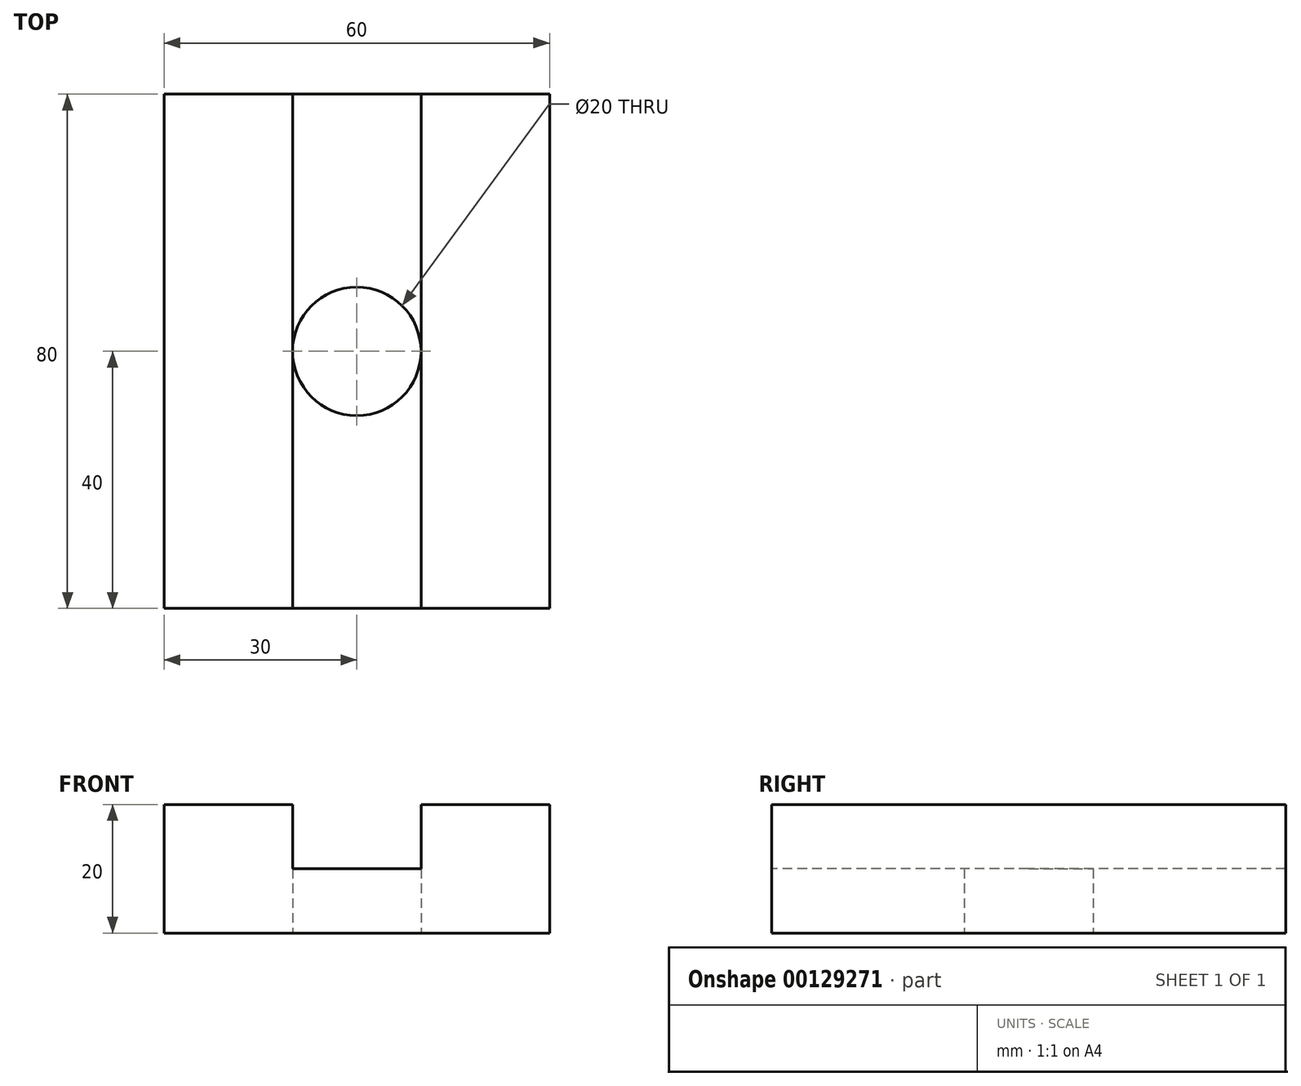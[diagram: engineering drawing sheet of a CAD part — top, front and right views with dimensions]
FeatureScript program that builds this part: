
annotation { "Feature Type Name" : "Feature", "Feature Type Description" : "" }
export const myFeature = defineFeature(function(context is Context, id is Id, definition is map)
    precondition{}
    {
        {
            var Q0;
            Q0=qCreatedBy(makeId("Front.planeOp"),FACE);
            var sketch = newSketch(context, id + "F0", { "sketchPlane" : qUnion([Q0])});
            skLineSegment(sketch, "E0", {"start": v(0, 0) * mm, "end": v(60, 0) * mm});
            skLineSegment(sketch, "E1", {"start": v(60, 0) * mm, "end": v(60, 20) * mm});
            skLineSegment(sketch, "E2", {"start": v(60, 20) * mm, "end": v(40, 20) * mm});
            skLineSegment(sketch, "E3", {"start": v(40, 20) * mm, "end": v(40, 10) * mm});
            skLineSegment(sketch, "E4", {"start": v(40, 10) * mm, "end": v(20, 10) * mm});
            skLineSegment(sketch, "E5", {"start": v(20, 10) * mm, "end": v(20, 20) * mm});
            skLineSegment(sketch, "E6", {"start": v(20, 20) * mm, "end": v(0, 20) * mm});
            skLineSegment(sketch, "E7", {"start": v(0, 20) * mm, "end": v(0, 0) * mm});
            skSolve(sketch);
        }
        {
            var Q0;
            Q0=makeQuery(id+"F0.imprint","IMPRINT",FACE,{"disambiguationData":[TD([[makeQuery(id+"F0.imprint","IMPRINT",EDGE,{"derivedFrom":sQuery(id+"F0.wireOp",EDGE,"E0")}),1.0]])]});
            extrude(context, id + "F1", {"entities" : qUnion([Q0]), "oppositeDirection" : true, "depth" : 80 * mm});
        }
        {
            var Q0;
            Q0=makeQuery(id+"F1.opExtrude","SWEPT_FACE",FACE,{"disambiguationData":[OSD([sQuery(id+"F0.wireOp",EDGE,"E0")])]});
            var sketch = newSketch(context, id + "F2", { "sketchPlane" : qUnion([Q0])});
            skCircle(sketch, "E8", {"center": v(30, -40) * mm, "radius": 10 * mm});
            skSolve(sketch);
        }
        {
            var Q0;
            Q0=makeQuery(id+"F2.imprint","IMPRINT",FACE,{"disambiguationData":[TD([[makeQuery(id+"F2.imprint","IMPRINT",EDGE,{"derivedFrom":sQuery(id+"F2.wireOp",EDGE,"E8")}),1.0]])]});
            var Q1;
            Q1=sQuery(id+"F2.wireOp",EDGE,"E8");
            extrude(context, id + "F3", {"entities" : qUnion([Q0]), "operationType" : NewBodyOperationType.REMOVE, "surfaceEntities" : qUnion([Q1]), "oppositeDirection" : true, "depth" : 20 * mm});
        }
    });
